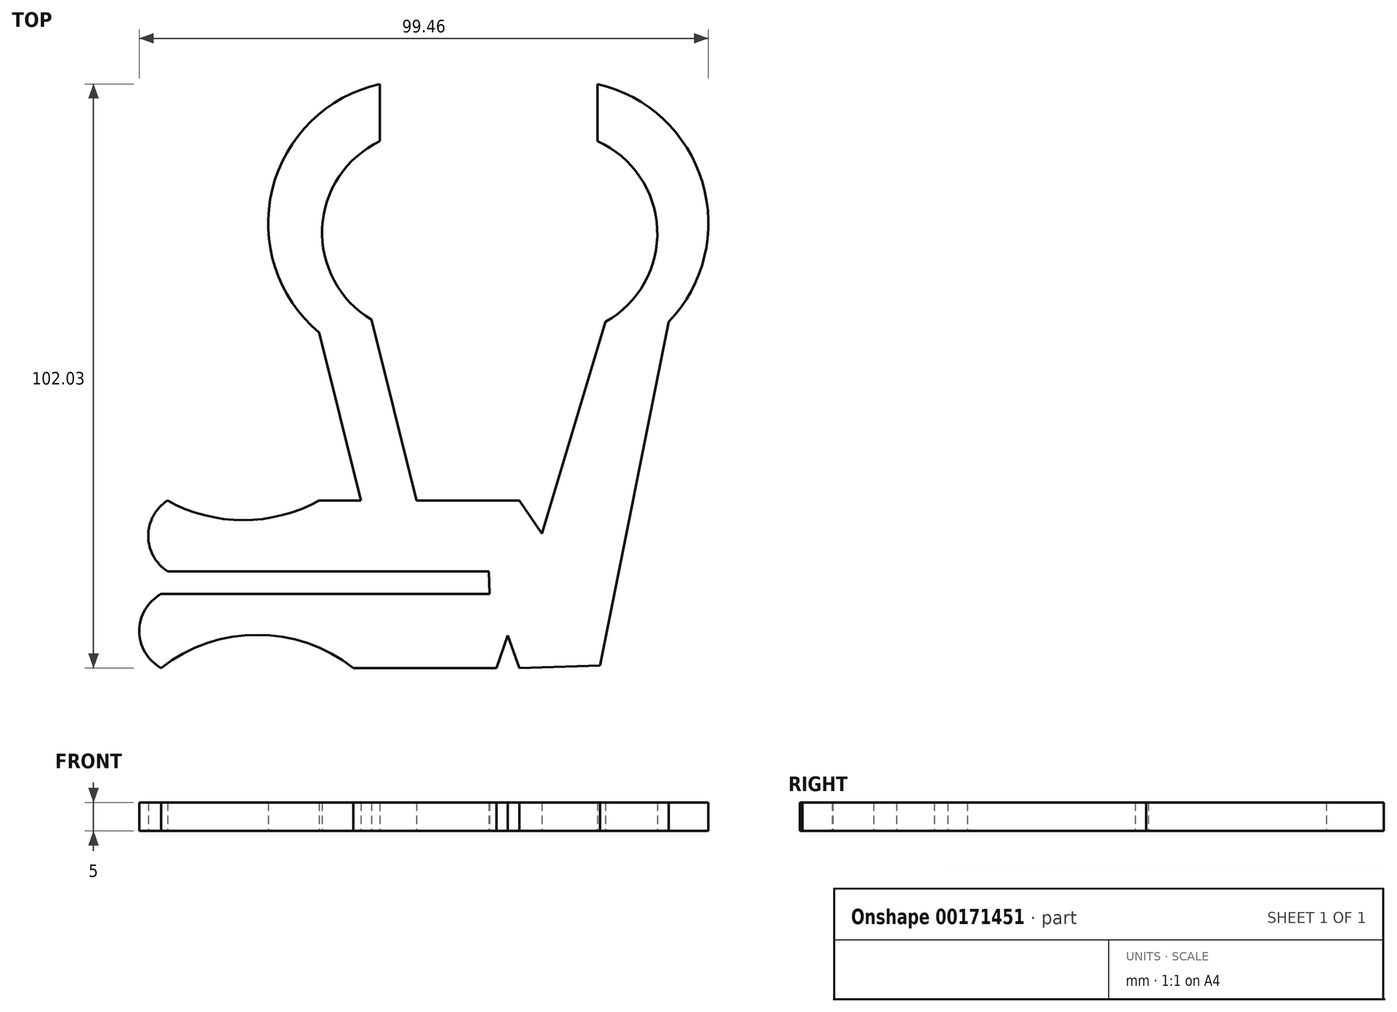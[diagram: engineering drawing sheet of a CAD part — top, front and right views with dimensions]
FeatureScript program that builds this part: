
annotation { "Feature Type Name" : "Feature", "Feature Type Description" : "" }
export const myFeature = defineFeature(function(context is Context, id is Id, definition is map)
    precondition{}
    {
        {
            var Q0;
            Q0=qCreatedBy(makeId("Top.planeOp"),FACE);
            var sketch = newSketch(context, id + "F0", { "sketchPlane" : qUnion([Q0])});
            skLineSegment(sketch, "E0", {"start": v(-4, -49.11) * mm, "end": v(-29, -49.11) * mm});
            skArc(sketch, "E1", {"start": v(-29, -49.11) * mm, "mid": v(-45.8, -43.35) * mm, "end": v(-62.59, -49.11) * mm});
            skArc(sketch, "E2", {"start": v(-62.59, -36.22) * mm, "mid": v(-66.4, -42.66) * mm, "end": v(-62.59, -49.11) * mm});
            skLineSegment(sketch, "E3", {"start": v(-62.59, -36.22) * mm, "end": v(-5.22, -36.22) * mm});
            skLineSegment(sketch, "E4.MirrorCS", {"start": v(-61.48, -32.22) * mm, "end": v(-5.33, -32.22) * mm});
            skArc(sketch, "E5.MirrorCS", {"start": v(-61.48, -32.22) * mm, "mid": v(-64.85, -26.04) * mm, "end": v(-61.48, -19.87) * mm});
            skArc(sketch, "E6.MirrorCS", {"start": v(-35, -19.87) * mm, "mid": v(-48.24, -23.29) * mm, "end": v(-61.48, -19.87) * mm});
            skLineSegment(sketch, "E7", {"start": v(-5.33, -32.22) * mm, "end": v(-5.22, -36.22) * mm});
            skPoint(sketch, "E8.endSnap0", {"position": v(-5.28, -34.22) * mm});
            skLineSegment(sketch, "E9", {"start": v(-27.65, -19.87) * mm, "end": v(-35, 9.48) * mm});
            skArc(sketch, "E10", {"start": v(-24.34, 52.92) * mm, "mid": v(-43.17, 34.51) * mm, "end": v(-35, 9.48) * mm});
            skLineSegment(sketch, "E11", {"start": v(-24.34, 52.92) * mm, "end": v(-24.34, 42.92) * mm});
            skArc(sketch, "E12", {"start": v(-24.34, 42.92) * mm, "mid": v(-34.45, 27.8) * mm, "end": v(-25.86, 11.77) * mm});
            skLineSegment(sketch, "E13", {"start": v(-25.86, 11.77) * mm, "end": v(-17.93, -19.87) * mm});
            skLineSegment(sketch, "E14.MirrorCS", {"start": v(13.67, 52.92) * mm, "end": v(13.67, 42.92) * mm});
            skArc(sketch, "E15.MirrorCS", {"start": v(13.67, 52.92) * mm, "mid": v(32, 35.78) * mm, "end": v(26.14, 11.38) * mm});
            skLineSegment(sketch, "E16.MirrorCS", {"start": v(15.07, 11.38) * mm, "end": v(5.7, -19.88) * mm});
            skArc(sketch, "E17.MirrorCS", {"start": v(13.67, 42.92) * mm, "mid": v(24.1, 27.58) * mm, "end": v(15.07, 11.38) * mm});
            skLineSegment(sketch, "E18", {"start": v(26.14, 11.38) * mm, "end": v(14.14, -48.68) * mm});
            skLineSegment(sketch, "E19", {"start": v(0, -49.11) * mm, "end": v(14.14, -48.68) * mm});
            skLineSegment(sketch, "E20", {"start": v(-35, -19.87) * mm, "end": v(-27.65, -19.87) * mm});
            skLineSegment(sketch, "E21", {"start": v(-17.93, -19.87) * mm, "end": v(-9.47, -19.88) * mm});
            skLineSegment(sketch, "E22", {"start": v(0, -19.88) * mm, "end": v(-9.47, -19.88) * mm});
            skLineSegment(sketch, "E23", {"start": v(-4, -49.11) * mm, "end": v(-2, -43.45) * mm});
            skLineSegment(sketch, "E24", {"start": v(-2, -43.45) * mm, "end": v(0, -49.11) * mm});
            skLineSegment(sketch, "E25", {"start": v(5.7, -19.88) * mm, "end": v(3.96, -25.65) * mm});
            skLineSegment(sketch, "E26", {"start": v(3.96, -25.65) * mm, "end": v(0, -19.88) * mm});
            skSolve(sketch);
        }
        {
            var Q0;
            Q0=makeQuery(id+"F0.imprint","IMPRINT",FACE,{"disambiguationData":[TD([[makeQuery(id+"F0.imprint","IMPRINT",EDGE,{"derivedFrom":sQuery(id+"F0.wireOp",EDGE,"E0")}),-1.0]])]});
            extrude(context, id + "F1", {"entities" : qUnion([Q0]), "depth" : 5 * mm});
        }
    });
